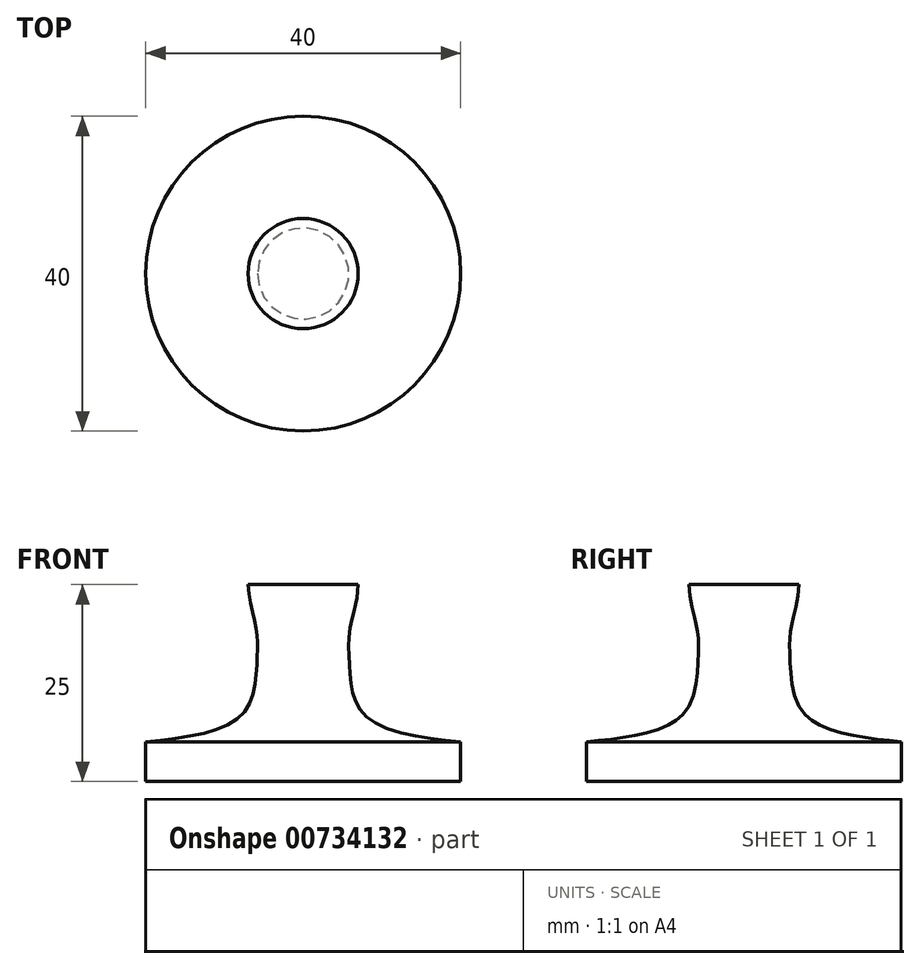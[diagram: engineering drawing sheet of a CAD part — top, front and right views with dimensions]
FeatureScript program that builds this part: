
annotation { "Feature Type Name" : "Feature", "Feature Type Description" : "" }
export const myFeature = defineFeature(function(context is Context, id is Id, definition is map)
    precondition{}
    {
        {
            var Q0;
            Q0=qCreatedBy(makeId("Front.planeOp"),FACE);
            var sketch = newSketch(context, id + "F0", { "sketchPlane" : qUnion([Q0])});
            skLineSegment(sketch, "E0", {"start": v(0, 0) * mm, "end": v(20, 0) * mm});
            skLineSegment(sketch, "E1", {"start": v(20, 0) * mm, "end": v(20, 5) * mm});
            skFitSpline(sketch, "E2", {"points": [v(20, 5) * mm, v(7.66, 8.6) * mm, v(5.86, 15.3) * mm, v(5.94, 19.2) * mm, v(7, 25) * mm], "startDerivative": vector(-44.06, 4.8) * mm, "endDerivative": vector(0.95, 26.8) * mm});
            skLineSegment(sketch, "E3", {"start": v(7, 25) * mm, "end": v(0, 25) * mm});
            skLineSegment(sketch, "E4", {"start": v(0, 25) * mm, "end": v(0, 0) * mm});
            skSolve(sketch);
        }
        {
            var Q0;
            Q0=qCreatedBy(makeId("Front.planeOp"),FACE);
            var sketch = newSketch(context, id + "F1", { "sketchPlane" : qUnion([Q0])});
            skLineSegment(sketch, "E5", {"start": v(0, 0) * mm, "end": v(0, 65) * mm});
            skSolve(sketch);
        }
        {
            var Q0;
            Q0=makeQuery(id+"F0.imprint","IMPRINT",FACE,{"disambiguationData":[TD([[makeQuery(id+"F0.imprint","IMPRINT",EDGE,{"derivedFrom":sQuery(id+"F0.wireOp",EDGE,"E0")}),1.0]])]});
            var Q1;
            Q1=sQuery(id+"F1.wireOp",EDGE,"E5");
            revolve(context, id + "F2", {"surfaceOperationType" : NewSurfaceOperationType.NEW, "entities" : qUnion([Q0]), "axis" : qUnion([Q1]), "revolveType" : RevolveType.FULL});
        }
    });
